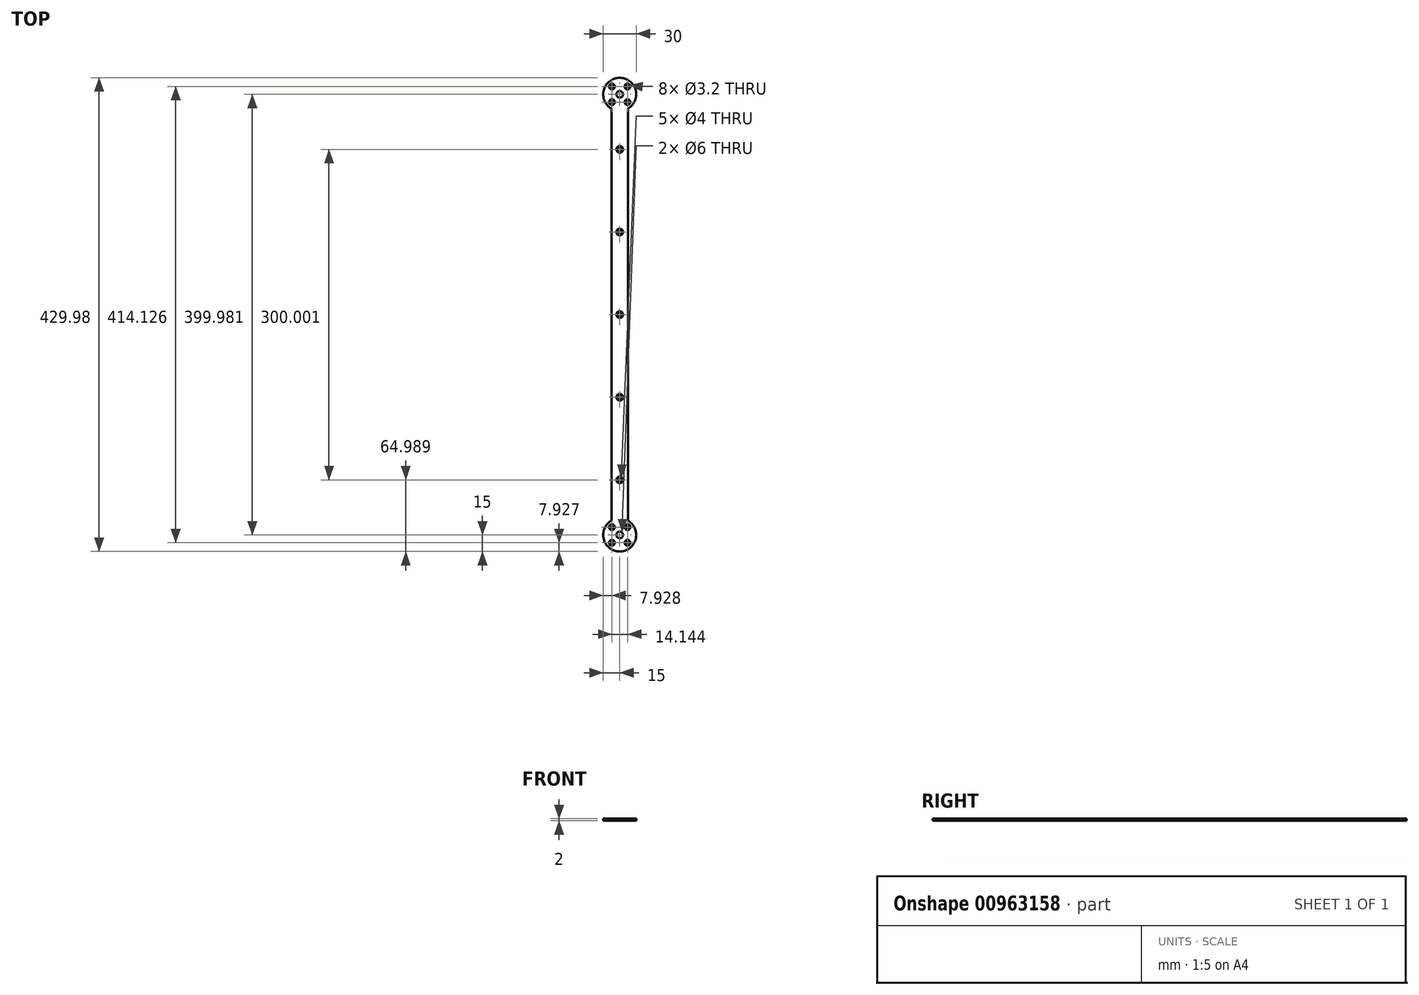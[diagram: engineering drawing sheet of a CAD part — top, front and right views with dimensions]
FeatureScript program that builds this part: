
annotation { "Feature Type Name" : "Feature", "Feature Type Description" : "" }
export const myFeature = defineFeature(function(context is Context, id is Id, definition is map)
    precondition{}
    {
        {
            var Q0;
            Q0=qCreatedBy(makeId("Top.planeOp"),FACE);
            var sketch = newSketch(context, id + "F0", { "sketchPlane" : qUnion([Q0])});
            skLineSegment(sketch, "E0.left", {"start": v(-15, 187) * mm, "end": v(-15, -187) * mm});
            skLineSegment(sketch, "E0.right", {"start": v(0, 187) * mm, "end": v(0, -187) * mm});
            skArc(sketch, "E1", {"start": v(-15, -187) * mm, "mid": v(-7.5, -214.99) * mm, "end": v(0, -187) * mm});
            skArc(sketch, "E2", {"start": v(0, 187) * mm, "mid": v(-7.5, 215) * mm, "end": v(-15, 187) * mm});
            skPoint(sketch, "E3.orphan", {"position": v(0, -199.99) * mm});
            skPoint(sketch, "E0.top.start.orphan", {"position": v(-15, -199.99) * mm});
            skPoint(sketch, "E4.orphan", {"position": v(-15, 200) * mm});
            skPoint(sketch, "E5.orphan", {"position": v(0, 200) * mm});
            skCircle(sketch, "E6", {"center": v(-7.5, 200) * mm, "radius": 3 * mm});
            skCircle(sketch, "E7", {"center": v(-7.5, -199.99) * mm, "radius": 3 * mm});
            skCircle(sketch, "E8", {"center": v(-14.57, 192.92) * mm, "radius": 1.6 * mm});
            skCircle(sketch, "E9.1.0", {"center": v(-0.43, 192.92) * mm, "radius": 1.6 * mm});
            skCircle(sketch, "E9.2.0", {"center": v(-0.43, 207.06) * mm, "radius": 1.6 * mm});
            skCircle(sketch, "E9.3.0", {"center": v(-14.57, 207.06) * mm, "radius": 1.6 * mm});
            skLineSegment(sketch, "E10", {"start": v(-7.5, 244.28) * mm, "end": v(-7.5, -231.8) * mm, "construction": true});
            skPoint(sketch, "E10.startSnap0", {"position": v(-7.5, 215) * mm});
            skCircle(sketch, "E11.MirrorC", {"center": v(-14.57, -192.92) * mm, "radius": 1.6 * mm});
            skCircle(sketch, "E12.MirrorC", {"center": v(-14.57, -207.06) * mm, "radius": 1.6 * mm});
            skCircle(sketch, "E13.MirrorC", {"center": v(-0.43, -192.92) * mm, "radius": 1.6 * mm});
            skCircle(sketch, "E14.MirrorC", {"center": v(-0.43, -207.06) * mm, "radius": 1.6 * mm});
            skCircle(sketch, "E15", {"center": v(-7.5, 0) * mm, "radius": 2 * mm});
            skPoint(sketch, "E15.centerSnap0", {"position": v(-15, 0) * mm});
            skCircle(sketch, "E16", {"center": v(-7.5, 75) * mm, "radius": 2 * mm});
            skCircle(sketch, "E17", {"center": v(-7.5, 150) * mm, "radius": 2 * mm});
            skCircle(sketch, "E18.MirrorC", {"center": v(-7.5, -150) * mm, "radius": 2 * mm});
            skCircle(sketch, "E19.MirrorC", {"center": v(-7.5, -75) * mm, "radius": 2 * mm});
            skSolve(sketch);
        }
        {
            var Q0;
            Q0=makeQuery(id+"F0.imprint","IMPRINT",FACE,{"disambiguationData":[TD([[makeQuery(id+"F0.imprint","IMPRINT",EDGE,{"derivedFrom":sQuery(id+"F0.wireOp",EDGE,"E0.left")}),1.0]])]});
            extrude(context, id + "F1", {"entities" : qUnion([Q0]), "depth" : 2 * mm, "offsetDistance" : 25 * mm});
        }
        {
            var Q0;
            Q0=makeQuery(id+"F1.opExtrude","CAP_EDGE",EDGE,{"disambiguationData":[OSD([sQuery(id+"F0.wireOp",EDGE,"E8")])],"isStart":false});
            chamfer(context, id + "F2", {"entities" : qUnion([Q0]), "width" : 1 * mm, "tangentPropagation" : true});
        }
        {
            var Q0;
            Q0=makeQuery(id+"F1.opExtrude","CAP_EDGE",EDGE,{"disambiguationData":[OSD([sQuery(id+"F0.wireOp",EDGE,"E9.3.0")])],"isStart":false});
            var Q1;
            Q1=makeQuery(id+"F1.opExtrude","CAP_EDGE",EDGE,{"disambiguationData":[OSD([sQuery(id+"F0.wireOp",EDGE,"E9.2.0")])],"isStart":false});
            var Q2;
            Q2=makeQuery(id+"F1.opExtrude","CAP_EDGE",EDGE,{"disambiguationData":[OSD([sQuery(id+"F0.wireOp",EDGE,"E9.1.0")])],"isStart":false});
            chamfer(context, id + "F3", {"entities" : qUnion([Q0, Q1, Q2]), "width" : 1 * mm, "tangentPropagation" : true});
        }
        {
            var Q0;
            Q0=makeQuery(id+"F1.opExtrude","CAP_EDGE",EDGE,{"disambiguationData":[OSD([sQuery(id+"F0.wireOp",EDGE,"E11.MirrorC")])],"isStart":false});
            var Q1;
            Q1=makeQuery(id+"F1.opExtrude","CAP_EDGE",EDGE,{"disambiguationData":[OSD([sQuery(id+"F0.wireOp",EDGE,"E12.MirrorC")])],"isStart":false});
            var Q2;
            Q2=makeQuery(id+"F1.opExtrude","CAP_EDGE",EDGE,{"disambiguationData":[OSD([sQuery(id+"F0.wireOp",EDGE,"E14.MirrorC")])],"isStart":false});
            var Q3;
            Q3=makeQuery(id+"F1.opExtrude","CAP_EDGE",EDGE,{"disambiguationData":[OSD([sQuery(id+"F0.wireOp",EDGE,"E13.MirrorC")])],"isStart":false});
            chamfer(context, id + "F4", {"entities" : qUnion([Q0, Q1, Q2, Q3]), "width" : 1 * mm, "tangentPropagation" : true});
        }
        {
            var Q0;
            Q0=makeQuery(id+"F1.opExtrude","CAP_EDGE",EDGE,{"disambiguationData":[OSD([sQuery(id+"F0.wireOp",EDGE,"E17")])],"isStart":false});
            var Q1;
            Q1=makeQuery(id+"F1.opExtrude","CAP_EDGE",EDGE,{"disambiguationData":[OSD([sQuery(id+"F0.wireOp",EDGE,"E16")])],"isStart":false});
            var Q2;
            Q2=makeQuery(id+"F1.opExtrude","CAP_EDGE",EDGE,{"disambiguationData":[OSD([sQuery(id+"F0.wireOp",EDGE,"E15")])],"isStart":false});
            var Q3;
            Q3=makeQuery(id+"F1.opExtrude","CAP_EDGE",EDGE,{"disambiguationData":[OSD([sQuery(id+"F0.wireOp",EDGE,"E19.MirrorC")])],"isStart":false});
            var Q4;
            Q4=makeQuery(id+"F1.opExtrude","CAP_EDGE",EDGE,{"disambiguationData":[OSD([sQuery(id+"F0.wireOp",EDGE,"E18.MirrorC")])],"isStart":false});
            chamfer(context, id + "F5", {"entities" : qUnion([Q0, Q1, Q2, Q3, Q4]), "width" : 1 * mm, "tangentPropagation" : true});
        }
    });
